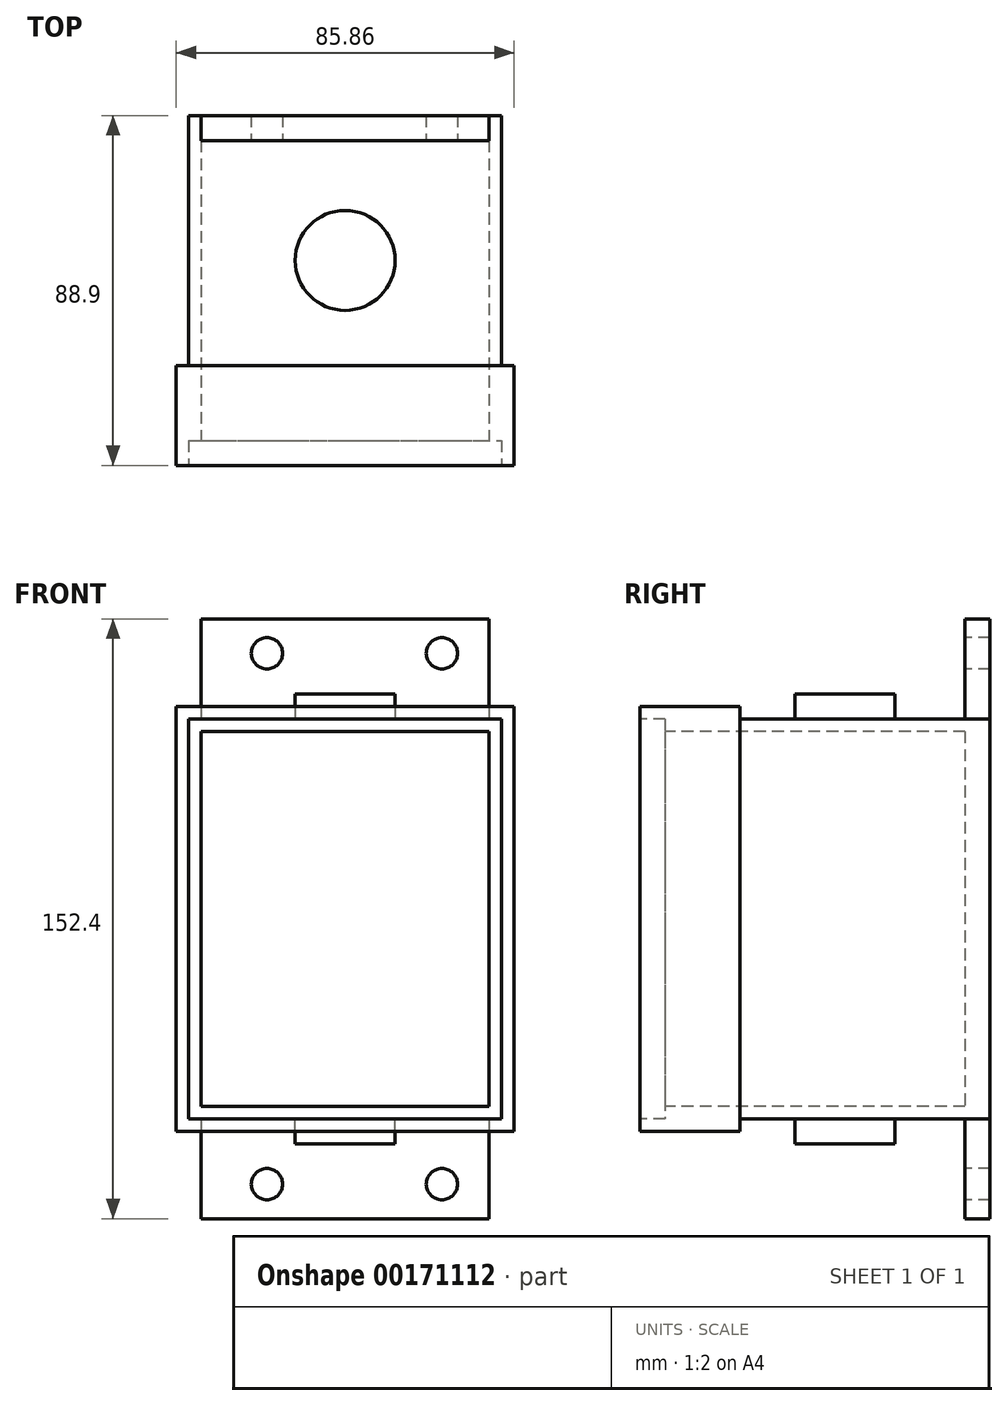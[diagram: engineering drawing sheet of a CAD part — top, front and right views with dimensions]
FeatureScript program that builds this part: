
annotation { "Feature Type Name" : "Feature", "Feature Type Description" : "" }
export const myFeature = defineFeature(function(context is Context, id is Id, definition is map)
    precondition{}
    {
        {
            var Q0;
            Q0=qCreatedBy(makeId("Front.planeOp"),FACE);
            var sketch = newSketch(context, id + "F0", { "sketchPlane" : qUnion([Q0])});
            skLineSegment(sketch, "E0.bottom", {"start": v(-39.75, 50.8) * mm, "end": v(39.75, 50.8) * mm});
            skLineSegment(sketch, "E0.top", {"start": v(-39.75, -50.8) * mm, "end": v(39.75, -50.8) * mm});
            skLineSegment(sketch, "E0.left", {"start": v(-39.75, 50.8) * mm, "end": v(-39.75, -50.8) * mm});
            skLineSegment(sketch, "E0.right", {"start": v(39.75, 50.8) * mm, "end": v(39.75, -50.8) * mm});
            skPoint(sketch, "E0.middle", {"position": v(0, 0) * mm});
            skSolve(sketch);
        }
        {
            var Q0;
            Q0 = qSketchRegion(id + "F0", true);
            extrude(context, id + "F1", {"entities" : qUnion([Q0]), "depth" : 88.9 * mm});
        }
        {
            var Q0;
            Q0=makeQuery(id+"F1.opExtrude","CAP_FACE",FACE,{"disambiguationData":[OSD([sQuery(id+"F0.wireOp",EDGE,"E0.bottom"),sQuery(id+"F0.wireOp",EDGE,"E0.top"),sQuery(id+"F0.wireOp",EDGE,"E0.left"),sQuery(id+"F0.wireOp",EDGE,"E0.right")])],"isStart":false});
            var sketch = newSketch(context, id + "F2", { "sketchPlane" : qUnion([Q0])});
            skLineSegment(sketch, "E1.bottom", {"start": v(-42.93, 53.98) * mm, "end": v(42.93, 53.98) * mm});
            skLineSegment(sketch, "E1.top", {"start": v(-42.93, -53.98) * mm, "end": v(42.93, -53.98) * mm});
            skLineSegment(sketch, "E1.left", {"start": v(-42.93, 53.98) * mm, "end": v(-42.93, -53.98) * mm});
            skLineSegment(sketch, "E1.right", {"start": v(42.93, 53.98) * mm, "end": v(42.93, -53.98) * mm});
            skPoint(sketch, "E1.middle", {"position": v(0, 0) * mm});
            skSolve(sketch);
        }
        {
            var Q0;
            Q0 = qSketchRegion(id + "F2", true);
            extrude(context, id + "F3", {"entities" : qUnion([Q0]), "operationType" : NewBodyOperationType.ADD, "oppositeDirection" : true, "depth" : 25.4 * mm});
        }
        {
            var Q0;
            Q0=makeQuery(id+"F3.boolean.opBoolean","MERGE",FACE,{"derivedFrom":[makeQuery(id+"F1.opExtrude","CAP_FACE",FACE,{"disambiguationData":[OSD([sQuery(id+"F0.wireOp",EDGE,"E0.bottom"),sQuery(id+"F0.wireOp",EDGE,"E0.top"),sQuery(id+"F0.wireOp",EDGE,"E0.left"),sQuery(id+"F0.wireOp",EDGE,"E0.right")])],"isStart":false}),makeQuery(id+"F3.opExtrude","CAP_FACE",FACE,{"disambiguationData":[OSD([sQuery(id+"F2.wireOp",EDGE,"E1.bottom"),sQuery(id+"F2.wireOp",EDGE,"E1.top"),sQuery(id+"F2.wireOp",EDGE,"E1.left"),sQuery(id+"F2.wireOp",EDGE,"E1.right")])],"isStart":true})]});
            var sketch = newSketch(context, id + "F4", { "sketchPlane" : qUnion([Q0])});
            skLineSegment(sketch, "E2.bottom", {"start": v(-36.58, 47.63) * mm, "end": v(36.58, 47.63) * mm});
            skLineSegment(sketch, "E2.top", {"start": v(-36.58, -47.63) * mm, "end": v(36.58, -47.63) * mm});
            skLineSegment(sketch, "E2.left", {"start": v(-36.58, 47.63) * mm, "end": v(-36.58, -47.63) * mm});
            skLineSegment(sketch, "E2.right", {"start": v(36.58, 47.63) * mm, "end": v(36.58, -47.63) * mm});
            skPoint(sketch, "E2.middle", {"position": v(0, 0) * mm});
            skSolve(sketch);
        }
        {
            var Q0;
            Q0 = qSketchRegion(id + "F4", true);
            extrude(context, id + "F5", {"entities" : qUnion([Q0]), "operationType" : NewBodyOperationType.REMOVE, "oppositeDirection" : true, "depth" : 85.72 * mm});
        }
        {
            var Q0;
            Q0=makeQuery(id+"F1.opExtrude","CAP_FACE",FACE,{"disambiguationData":[OSD([sQuery(id+"F0.wireOp",EDGE,"E0.bottom"),sQuery(id+"F0.wireOp",EDGE,"E0.top"),sQuery(id+"F0.wireOp",EDGE,"E0.left"),sQuery(id+"F0.wireOp",EDGE,"E0.right")])],"isStart":true});
            var sketch = newSketch(context, id + "F6", { "sketchPlane" : qUnion([Q0])});
            skLineSegment(sketch, "E3.bottom", {"start": v(-36.58, 76.2) * mm, "end": v(36.58, 76.2) * mm});
            skLineSegment(sketch, "E3.top", {"start": v(-36.58, -76.2) * mm, "end": v(36.58, -76.2) * mm});
            skLineSegment(sketch, "E3.left", {"start": v(-36.58, 76.2) * mm, "end": v(-36.58, -76.2) * mm});
            skLineSegment(sketch, "E3.right", {"start": v(36.58, 76.2) * mm, "end": v(36.58, -76.2) * mm});
            skPoint(sketch, "E3.middle", {"position": v(0, 0) * mm});
            skSolve(sketch);
        }
        {
            var Q0;
            Q0 = qSketchRegion(id + "F6", true);
            extrude(context, id + "F7", {"entities" : qUnion([Q0]), "operationType" : NewBodyOperationType.ADD, "oppositeDirection" : true, "depth" : 6.35 * mm});
        }
        {
            var Q0;
            {var subQ0=sQuery(id+"F6.wireOp",EDGE,"E3.bottom");var subQ1=sQuery(id+"F6.wireOp",EDGE,"E3.left");var subQ2=sQuery(id+"F6.wireOp",EDGE,"E3.right");Q0=makeQuery(id+"F7.boolean.opBoolean","SPLIT",FACE,{"disambiguationData":[TD([makeQuery(id+"F1.opExtrude","SWEPT_FACE",FACE,{"disambiguationData":[OSD([sQuery(id+"F0.wireOp",EDGE,"E0.bottom")])]})])],"derivedFrom":makeQuery(id+"F7.opExtrude","CAP_FACE",FACE,{"disambiguationData":[OSD([subQ0,sQuery(id+"F6.wireOp",EDGE,"E3.top"),subQ1,subQ2])],"isStart":false})});}
            var sketch = newSketch(context, id + "F8", { "sketchPlane" : qUnion([Q0])});
            skCircle(sketch, "E4", {"center": v(-19.88, 67.44) * mm, "radius": 3.97 * mm});
            skCircle(sketch, "E5", {"center": v(24.57, 67.44) * mm, "radius": 3.97 * mm});
            skCircle(sketch, "E6", {"center": v(-19.88, -67.44) * mm, "radius": 3.97 * mm});
            skCircle(sketch, "E7", {"center": v(24.57, -67.44) * mm, "radius": 3.97 * mm});
            skLineSegment(sketch, "E8", {"start": v(0, 76.2) * mm, "end": v(0, -76.14) * mm});
            skPoint(sketch, "E8.endSnap0", {"position": v(0, 76.2) * mm});
            skSolve(sketch);
        }
        {
            var Q0;
            Q0 = qSketchRegion(id + "F8", true);
            extrude(context, id + "F9", {"entities" : qUnion([Q0]), "operationType" : NewBodyOperationType.REMOVE, "endBound" : BoundingType.THROUGH_ALL, "oppositeDirection" : true, "depth" : 25.4 * mm});
        }
        {
            var Q0;
            Q0=makeQuery(id+"F3.boolean.opBoolean","MERGE",FACE,{"derivedFrom":[makeQuery(id+"F1.opExtrude","CAP_FACE",FACE,{"disambiguationData":[OSD([sQuery(id+"F0.wireOp",EDGE,"E0.bottom"),sQuery(id+"F0.wireOp",EDGE,"E0.top"),sQuery(id+"F0.wireOp",EDGE,"E0.left"),sQuery(id+"F0.wireOp",EDGE,"E0.right")])],"isStart":false}),makeQuery(id+"F3.opExtrude","CAP_FACE",FACE,{"disambiguationData":[OSD([sQuery(id+"F2.wireOp",EDGE,"E1.bottom"),sQuery(id+"F2.wireOp",EDGE,"E1.top"),sQuery(id+"F2.wireOp",EDGE,"E1.left"),sQuery(id+"F2.wireOp",EDGE,"E1.right")])],"isStart":true})]});
            var sketch = newSketch(context, id + "F10", { "sketchPlane" : qUnion([Q0])});
            skLineSegment(sketch, "E9.bottom", {"start": v(-39.75, 50.8) * mm, "end": v(39.75, 50.8) * mm});
            skLineSegment(sketch, "E9.top", {"start": v(-39.75, -50.8) * mm, "end": v(39.75, -50.8) * mm});
            skLineSegment(sketch, "E9.left", {"start": v(-39.75, 50.8) * mm, "end": v(-39.75, -50.8) * mm});
            skLineSegment(sketch, "E9.right", {"start": v(39.75, 50.8) * mm, "end": v(39.75, -50.8) * mm});
            skPoint(sketch, "E9.middle", {"position": v(0, 0) * mm});
            skLineSegment(sketch, "E10.bottom", {"start": v(-36.58, 47.63) * mm, "end": v(36.58, 47.63) * mm});
            skLineSegment(sketch, "E10.top", {"start": v(-36.58, -47.63) * mm, "end": v(36.58, -47.63) * mm});
            skLineSegment(sketch, "E10.left", {"start": v(-36.58, 47.63) * mm, "end": v(-36.58, -47.63) * mm});
            skLineSegment(sketch, "E10.right", {"start": v(36.58, 47.63) * mm, "end": v(36.58, -47.63) * mm});
            skSolve(sketch);
        }
        {
            var Q0;
            Q0 = qSketchRegion(id + "F10", true);
            extrude(context, id + "F11", {"entities" : qUnion([Q0]), "operationType" : NewBodyOperationType.REMOVE, "oppositeDirection" : true, "depth" : 6.35 * mm});
        }
        {
            var Q0;
            Q0=makeQuery(id+"F1.opExtrude","SWEPT_FACE",FACE,{"disambiguationData":[OSD([sQuery(id+"F0.wireOp",EDGE,"E0.bottom")])]});
            var sketch = newSketch(context, id + "F12", { "sketchPlane" : qUnion([Q0])});
            skCircle(sketch, "E11", {"center": v(0, -36.83) * mm, "radius": 12.7 * mm});
            skSolve(sketch);
        }
        {
            var Q0;
            Q0 = qSketchRegion(id + "F12", true);
            extrude(context, id + "F13", {"entities" : qUnion([Q0]), "operationType" : NewBodyOperationType.ADD, "depth" : 6.35 * mm});
        }
        {
            var Q0;
            Q0=makeQuery(id+"F1.opExtrude","SWEPT_FACE",FACE,{"disambiguationData":[OSD([sQuery(id+"F0.wireOp",EDGE,"E0.top")])]});
            var sketch = newSketch(context, id + "F14", { "sketchPlane" : qUnion([Q0])});
            skCircle(sketch, "E12", {"center": v(0, 36.83) * mm, "radius": 12.7 * mm});
            skSolve(sketch);
        }
        {
            var Q0;
            Q0 = qSketchRegion(id + "F14", true);
            extrude(context, id + "F15", {"entities" : qUnion([Q0]), "operationType" : NewBodyOperationType.ADD, "depth" : 6.35 * mm});
        }
    });
